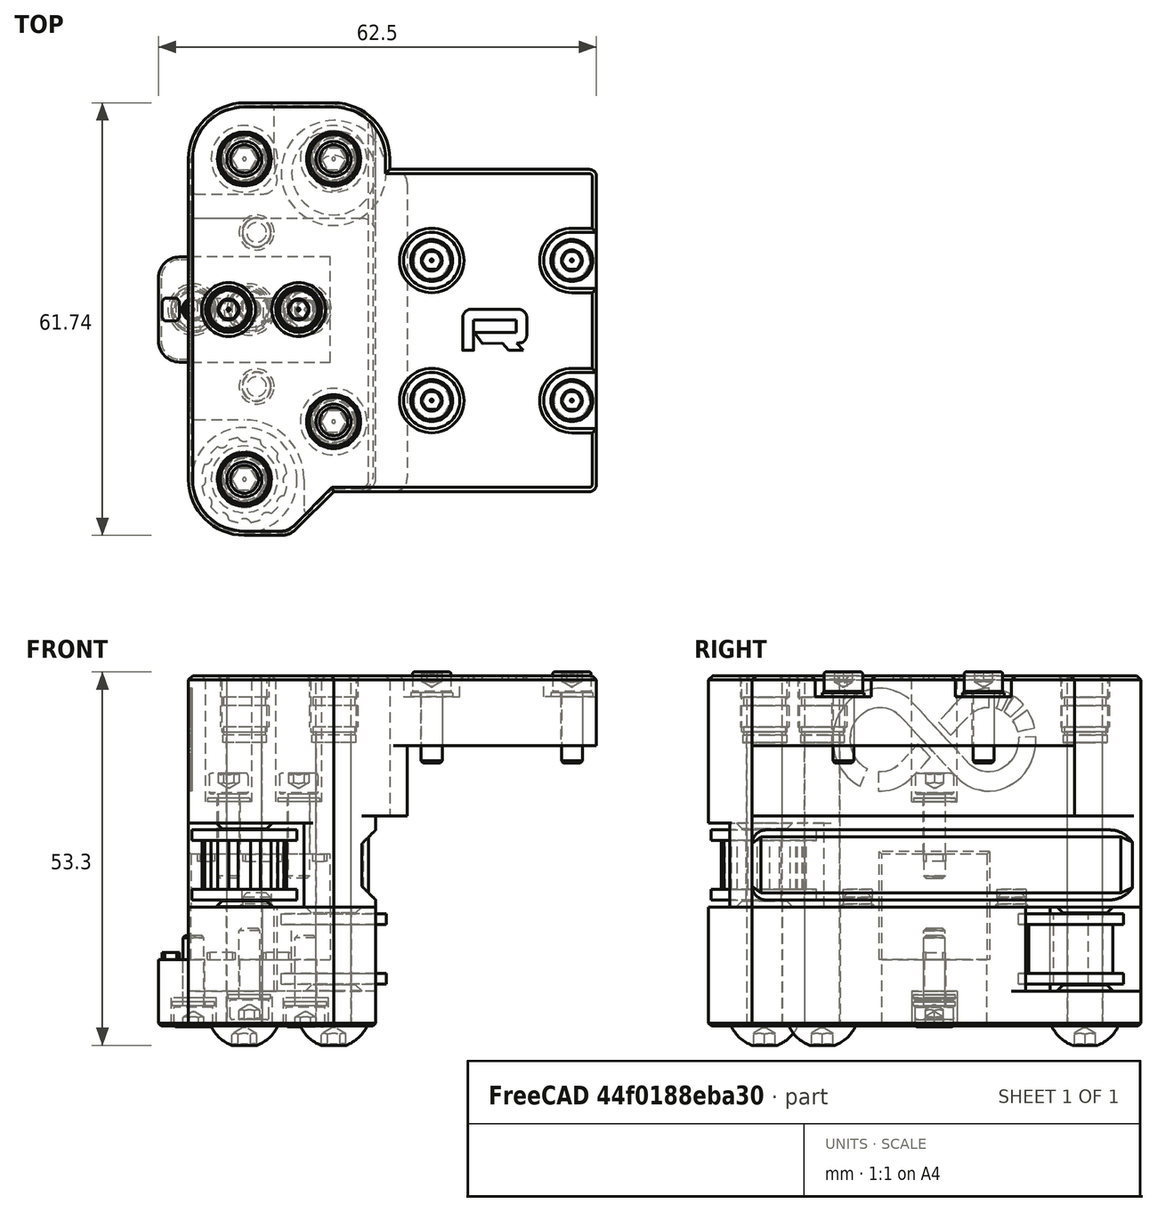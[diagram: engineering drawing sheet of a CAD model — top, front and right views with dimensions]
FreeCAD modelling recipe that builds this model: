
FCSTD DOCUMENT  (FreeCAD 0.19R24291 (Git))
Label: y-carrier-right-1515-assembly
License: Other
LicenseURL: GPL3
objects: Part::FeaturePython×26, Part::Feature×4, Spreadsheet::Sheet×2, PartDesign::CoordinateSystem×1, App::Part×1
note: 31 computed .brp shape members not serialized (recipe doc carries the construction recipe); baked Part::Feature solids carry a one-line shape summary decoded from their .brp

FEATURE [Part::Feature] Part__Mirroring002001  label="20t-idler"
  Placement = pos=(0,-4.61,0) rot=(0,0,1;0rad)
  shape: bbox 15 x 15 x 10 mm, 31 faces (baked)
FEATURE [Part::Feature] Part__Mirroring003001  label="smooth-idler-6mm"
  Placement = pos=(2,0.5,0) rot=(0,0,1;0rad)
  shape: bbox 15 x 15 x 10 mm, 8 faces (baked)
FEATURE [Part::FeaturePython] Screw002  label="M5x50-Screw"  # Fasteners workbench fastener (typed FeaturePython)
  Placement = pos=(-9,21.5,3) rot=(1,0,0;3.14159rad)
  diameter = 3
  invert = false
  length = 11
  lengthCustom = 50
  matchOuter = true
  offset = 0
  thread = false
  type = 39
FEATURE [Part::FeaturePython] Screw003  label="M5x50-Screw004"  # Fasteners workbench fastener (typed FeaturePython)
  Placement = pos=(-21.74,21.5,3) rot=(1,0,0;3.14159rad)
  diameter = 3
  invert = false
  length = 11
  lengthCustom = 50
  matchOuter = true
  offset = 0
  thread = false
  type = 39
FEATURE [Part::FeaturePython] Screw004  label="M5x50-Screw005"  # Fasteners workbench fastener (typed FeaturePython)
  Placement = pos=(-9,-16,3) rot=(1,0,0;3.14159rad)
  diameter = 3
  invert = false
  length = 11
  lengthCustom = 50
  matchOuter = true
  offset = 0
  thread = false
  type = 39
FEATURE [Part::FeaturePython] Screw005  label="M5x50-Screw006"  # Fasteners workbench fastener (typed FeaturePython)
  Placement = pos=(-21.74,-24.24,3) rot=(1,0,0;3.14159rad)
  diameter = 3
  invert = false
  length = 11
  lengthCustom = 50
  matchOuter = true
  offset = 0
  thread = false
  type = 39
FEATURE [Part::FeaturePython] Washer002  label="M3-Washer"  # Fasteners workbench fastener (typed FeaturePython)
  Placement = pos=(25,7,50) rot=(0,0,1;0rad)
  diameter = 4
  invert = true
  matchOuter = true
  offset = 0
  type = 5
FEATURE [Part::FeaturePython] Washer003  label="M3-Washer007"  # Fasteners workbench fastener (typed FeaturePython)
  Placement = pos=(25,-13,50) rot=(0,0,1;0rad)
  diameter = 4
  invert = true
  matchOuter = true
  offset = 0
  type = 5
FEATURE [Part::FeaturePython] Washer004  label="M3-Washer009"  # Fasteners workbench fastener (typed FeaturePython)
  Placement = pos=(5,-13,50) rot=(0,0,1;0rad)
  diameter = 4
  invert = true
  matchOuter = true
  offset = 0
  type = 5
FEATURE [Part::FeaturePython] Washer005  label="M3-Washer008"  # Fasteners workbench fastener (typed FeaturePython)
  Placement = pos=(5,7,50) rot=(0,0,1;0rad)
  diameter = 4
  invert = true
  matchOuter = true
  offset = 0
  type = 5
FEATURE [Part::FeaturePython] Screw006  label="M3x10-Screw"  # Fasteners workbench fastener (typed FeaturePython)
  Placement = pos=(25,-13,50.55) rot=(0,0,1;0rad)
  baseObject = -> Washer003 [Edge1]
  diameter = 4
  invert = false
  length = 3
  lengthCustom = 10
  matchOuter = true
  offset = 0
  thread = false
  type = 33
FEATURE [Part::FeaturePython] Screw007  label="M3x10-Screw005"  # Fasteners workbench fastener (typed FeaturePython)
  Placement = pos=(5,-13,50.55) rot=(0,0,1;0rad)
  baseObject = -> Washer004 [Edge1]
  diameter = 4
  invert = false
  length = 3
  lengthCustom = 10
  matchOuter = true
  offset = 0
  thread = false
  type = 33
FEATURE [Part::FeaturePython] Screw008  label="M3x10-Screw004"  # Fasteners workbench fastener (typed FeaturePython)
  Placement = pos=(5,7,50.55) rot=(0,0,1;0rad)
  baseObject = -> Washer005 [Edge1]
  diameter = 4
  invert = false
  length = 3
  lengthCustom = 10
  matchOuter = true
  offset = 0
  thread = false
  type = 33
FEATURE [Part::FeaturePython] Screw009  label="M3x10-Screw003"  # Fasteners workbench fastener (typed FeaturePython)
  Placement = pos=(25,7,50.55) rot=(0,0,1;0rad)
  baseObject = -> Washer002 [Edge1]
  diameter = 4
  invert = false
  length = 3
  lengthCustom = 10
  matchOuter = true
  offset = 0
  thread = false
  type = 33
FEATURE [Part::Feature] Chamfer010001  label="y-carrier-bottom-right"
  Placement = pos=(0,0,3) rot=(0,0,1;0rad)
  shape: bbox 31 x 61.74 x 19 mm, 118 faces (baked)
FEATURE [Part::Feature] Cut001001  label="y-carrier-top-right"
  Placement = pos=(0,0,3) rot=(0,0,1;0rad)
  shape: bbox 58.24 x 61.74 x 33.85 mm, 483 faces (baked)
FEATURE [Part::FeaturePython] Washer008  label="M3-Washer023"  # Fasteners workbench fastener (typed FeaturePython)
  Placement = pos=(-13,0,6.45) rot=(1,0,0;3.14159rad)
  diameter = 4
  invert = false
  matchOuter = true
  offset = 0
  type = 5
FEATURE [Part::FeaturePython] Washer009  label="M3-Washer022"  # Fasteners workbench fastener (typed FeaturePython)
  Placement = pos=(-21,0,7.45) rot=(1,0,0;3.14159rad)
  diameter = 4
  invert = false
  matchOuter = true
  offset = 0
  type = 5
FEATURE [Part::FeaturePython] Washer010  label="M3-Washer021"  # Fasteners workbench fastener (typed FeaturePython)
  Placement = pos=(-29,0,6.45) rot=(1,0,0;3.14159rad)
  diameter = 4
  invert = false
  matchOuter = true
  offset = 0
  type = 5
FEATURE [Part::FeaturePython] Screw  label="M3x10-Screw013"  # Fasteners workbench fastener (typed FeaturePython)
  Placement = pos=(-13,0,5.9) rot=(1,0,0;3.14159rad)
  baseObject = -> Washer008 [Edge1]
  diameter = 4
  invert = false
  length = 3
  lengthCustom = 10
  matchOuter = true
  offset = 0
  thread = false
  type = 33
FEATURE [Part::FeaturePython] Screw010  label="M3x10-Screw011"  # Fasteners workbench fastener (typed FeaturePython)
  Placement = pos=(-29,0,5.9) rot=(1,0,0;3.14159rad)
  baseObject = -> Washer010 [Edge1]
  diameter = 4
  invert = false
  length = 3
  lengthCustom = 10
  matchOuter = true
  offset = 0
  thread = false
  type = 33
FEATURE [Part::FeaturePython] Screw011  label="M3x10-Screw012"  # Fasteners workbench fastener (typed FeaturePython)
  Placement = pos=(-21,0,6.9) rot=(1,0,0;3.14159rad)
  baseObject = -> Washer009 [Edge1]
  diameter = 4
  invert = false
  length = 3
  lengthCustom = 10
  matchOuter = true
  offset = 0
  thread = false
  type = 33
FEATURE [Part::FeaturePython] Washer011  label="M3-Washer014"  # Fasteners workbench fastener (typed FeaturePython)
  Placement = pos=(-14,0,35) rot=(0,0,1;0rad)
  baseObject = -> Cut001001 [Edge1162]
  diameter = 4
  invert = false
  matchOuter = true
  offset = 0
  type = 5
FEATURE [Part::FeaturePython] Washer012  label="M3-Washer015"  # Fasteners workbench fastener (typed FeaturePython)
  Placement = pos=(-24,0,35) rot=(0,0,1;0rad)
  baseObject = -> Cut001001 [Edge1160]
  diameter = 4
  invert = false
  matchOuter = true
  offset = 0
  type = 5
FEATURE [Part::FeaturePython] Screw012  label="M3x12-Screw"  # Fasteners workbench fastener (typed FeaturePython)
  Placement = pos=(-14,0,36.1) rot=(0,0,1;0rad)
  diameter = 4
  invert = false
  length = 4
  lengthCustom = 12
  matchOuter = true
  offset = 0
  thread = false
  type = 33
FEATURE [Part::FeaturePython] Screw013  label="M3x12-Screw001"  # Fasteners workbench fastener (typed FeaturePython)
  Placement = pos=(-24,0,36.1) rot=(0,0,1;0rad)
  diameter = 4
  invert = false
  length = 4
  lengthCustom = 12
  matchOuter = true
  offset = 0
  thread = false
  type = 33
FEATURE [Part::FeaturePython] HeatSet  label="M5-HeatSet"  # WARN: FeaturePython — macro-defined, semantics opaque (R4)
  Placement = pos=(-9,21.5,53) rot=(0,0,1;0rad)
  baseObject = -> Cut001001 [Edge931]
  diameter = 5
  invert = true
  offset = 0
FEATURE [Part::FeaturePython] HeatSet001  label="M5-HeatSet001"  # WARN: FeaturePython — macro-defined, semantics opaque (R4)
  Placement = pos=(-21.74,21.5,53) rot=(0,0,1;0rad)
  baseObject = -> Cut001001 [Edge932]
  diameter = 5
  invert = true
  offset = 0
FEATURE [Part::FeaturePython] HeatSet002  label="M5-HeatSet002"  # WARN: FeaturePython — macro-defined, semantics opaque (R4)
  Placement = pos=(-9,-16,53) rot=(0,0,1;0rad)
  baseObject = -> Cut001001 [Edge926]
  diameter = 5
  invert = true
  offset = 0
FEATURE [Part::FeaturePython] HeatSet003  label="M5-HeatSet003"  # WARN: FeaturePython — macro-defined, semantics opaque (R4)
  Placement = pos=(-21.74,-24.24,53) rot=(0,0,1;0rad)
  baseObject = -> Cut001001 [Edge927]
  diameter = 5
  invert = true
  offset = 0
FEATURE [PartDesign::CoordinateSystem] LCS_Y_carrier_right  label="LCS_Y-carrier-right"
  AttacherType = Attacher::AttachEngine3D
FEATURE [App::Part] Part  label="Y-carrier-right"
  Group = -> [Part__Mirroring002001,Part__Mirroring003001,Screw003,Screw004,Screw005,Screw002,Screw006,Screw009,Screw008,Screw007,Washer005,Washer004,Washer003,Washer002,Chamfer010001,Cut001001,Washer010,Screw010,Washer008,Screw011,Washer009,Screw,Washer012,Screw013,Screw012,Washer011,HeatSet,HeatSet001,HeatSet002,HeatSet003,LCS_Y_carrier_right]
  Origin = -> Origin
FEATURE [Spreadsheet::Sheet] Fasteners_BOM
  cells = A1=Type; B1=Qty; A2=Heat Set Insert M5; B2=8; A3=ISO4762 Screw M3x10; B3=14; A4=ISO4762 Screw M3x12; B4=4; A5=ISO7092 Washer M3; B5=32; A6=ISO7380-1 Screw M5x50; B6=8
FEATURE [Spreadsheet::Sheet] Fasteners_BOM001
  cells = A1=Type; B1=Qty; A2=Heat Set Insert M5; B2=8; A3=ISO4762 Screw M3x10; B3=14; A4=ISO4762 Screw M3x12; B4=4; A5=ISO7092 Washer M3; B5=32; A6=ISO7380-1 Screw M5x50; B6=8
